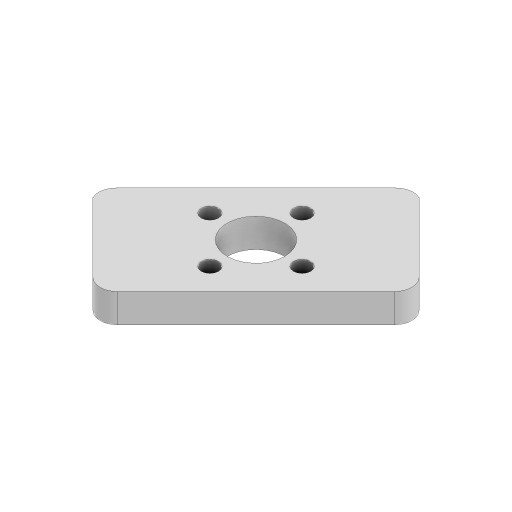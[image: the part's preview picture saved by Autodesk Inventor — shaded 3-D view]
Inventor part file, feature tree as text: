
AUTODESK INVENTOR PART (.ipt)
format: ipt  version: 2023 (Build 270158000, 158)  size: 959,488 bytes
history: native  units: mm
features: sketch x5, extrude x4, fillet x3, chamfer x1, mirror x1
ambient origin geometry x8: Origin, YZ Plane, XZ Plane, XY Plane, X Axis, Y Axis, Z Axis, Center Point
bodies: Solid1 (feature_tree)
feature tree (14):
  extrude  "Extrusion1"  Depth=3.0mm
  extrude  "Extrusion2"  Depth=10.0mm TaperAngle=0.0deg
  sketch  "Sketch4"  dims[d7=3.0mm]
  chamfer  "Chamfer1"  Distance=10.0mm
  fillet  "Fillet1"  Radius=2.0mm
  fillet  "Fillet2"  Radius=3.0mm
  extrude  "Extrusion3"  Depth=7.0mm
  fillet  "Fillet3"  Radius=10.0mm
  extrude  "Extrusion4"  Depth=3.0mm
  sketch  "Sketch2"  dims[d2=20.0mm d3=3.0mm]
  sketch  "Sketch3"  dims[d4=20.0mm d5=10.0mm d6=0.0mm]
  sketch  "Sketch5"  dims[d8=18.5mm]
  sketch  "Sketch6"  dims[d9=20.0mm d10=10.0mm d11=0.0mm d12=6.0mm d13=2.0mm d14=45.0deg d15=3.0mm d16=7.0mm d17=10.0mm d18=0.0mm d19=3.0mm d20=5.5mm d21=0.0mm]
  mirror  "Mirror7"
